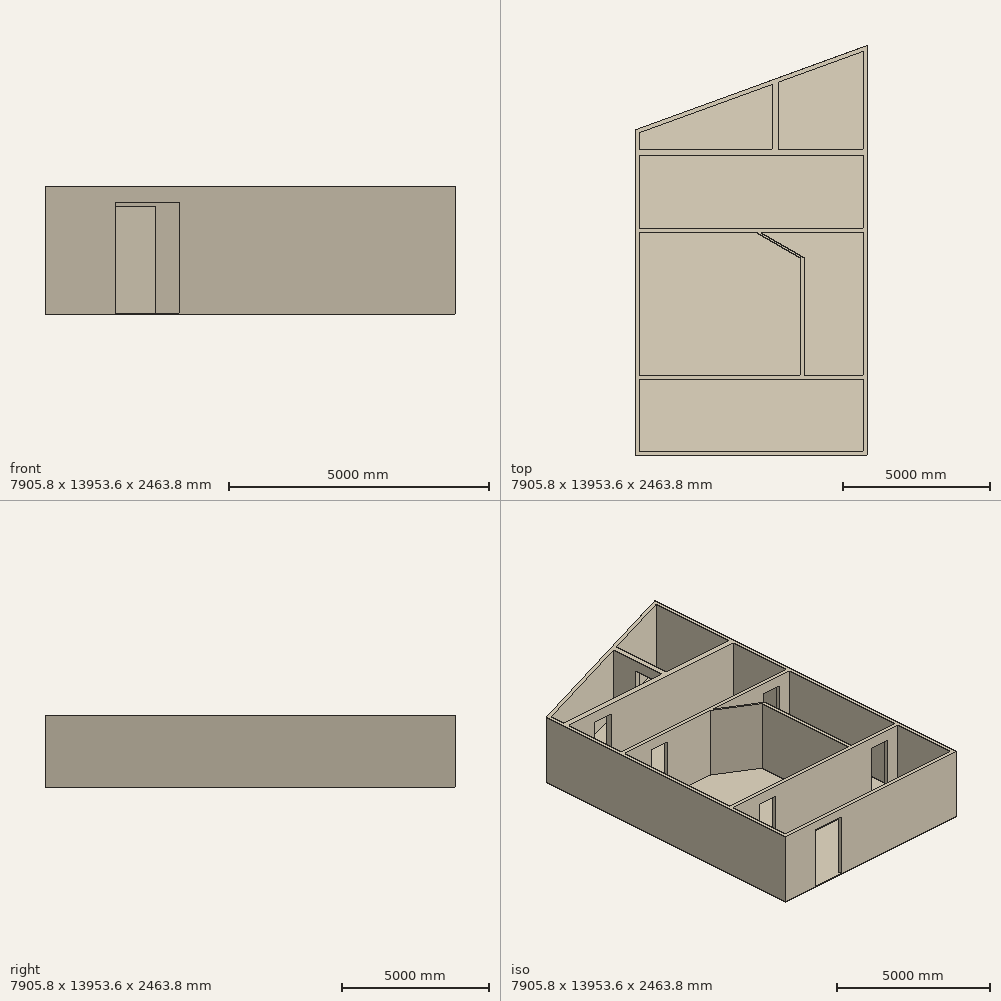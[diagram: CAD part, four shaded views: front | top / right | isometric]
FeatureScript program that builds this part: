
annotation { "Feature Type Name" : "Feature", "Feature Type Description" : "" }
export const myFeature = defineFeature(function(context is Context, id is Id, definition is map)
    precondition{}
    {
        {
            var Q0;
            Q0=qCreatedBy(makeId("Top.planeOp"),FACE);
            var sketch = newSketch(context, id + "F0", { "sketchPlane" : qUnion([Q0])});
            skLineSegment(sketch, "E0", {"start": v(0, 0) * mm, "end": v(0, -11076.15) * mm});
            skLineSegment(sketch, "E1", {"start": v(0, -11076.15) * mm, "end": v(7905.75, -11076.15) * mm});
            skLineSegment(sketch, "E2", {"start": v(7905.75, -11076.15) * mm, "end": v(7905.75, 2877.46) * mm});
            skLineSegment(sketch, "E3", {"start": v(7905.75, 2877.46) * mm, "end": v(0, 0) * mm});
            skLineSegment(sketch, "E4.0", {"start": v(139.7, -97.82) * mm, "end": v(139.7, -10936.45) * mm});
            skLineSegment(sketch, "E4.1", {"start": v(7766.05, 2677.95) * mm, "end": v(139.7, -97.82) * mm});
            skLineSegment(sketch, "E4.2", {"start": v(7766.05, -10936.45) * mm, "end": v(7766.05, 2677.95) * mm});
            skLineSegment(sketch, "E4.3", {"start": v(139.7, -10936.45) * mm, "end": v(7766.05, -10936.45) * mm});
            skLineSegment(sketch, "E5", {"start": v(139.7, -8498.05) * mm, "end": v(7766.05, -8498.05) * mm});
            skLineSegment(sketch, "E6", {"start": v(139.7, -8358.35) * mm, "end": v(7766.05, -8358.35) * mm});
            skLineSegment(sketch, "E7", {"start": v(139.7, -3341.85) * mm, "end": v(7766.05, -3341.85) * mm});
            skLineSegment(sketch, "E8", {"start": v(139.7, -3481.55) * mm, "end": v(7766.05, -3481.55) * mm});
            skLineSegment(sketch, "E9", {"start": v(139.7, -674.85) * mm, "end": v(7766.05, -674.85) * mm});
            skLineSegment(sketch, "E10", {"start": v(139.7, -878.05) * mm, "end": v(7766.05, -878.05) * mm});
            skLineSegment(sketch, "E11", {"start": v(4667.25, -674.85) * mm, "end": v(4667.25, 1550.07) * mm});
            skLineSegment(sketch, "E12", {"start": v(4870.45, -674.85) * mm, "end": v(4870.45, 1624.03) * mm});
            skLineSegment(sketch, "E13", {"start": v(5626.1, -4361.44) * mm, "end": v(5626.1, -8358.35) * mm});
            skLineSegment(sketch, "E14", {"start": v(5765.8, -4361.44) * mm, "end": v(5765.8, -8358.35) * mm});
            skLineSegment(sketch, "E15", {"start": v(5626.1, -4361.44) * mm, "end": v(5765.8, -4361.44) * mm});
            skLineSegment(sketch, "E16", {"start": v(5626.1, -4361.44) * mm, "end": v(4102.1, -3481.55) * mm});
            skLineSegment(sketch, "E17", {"start": v(4102.1, -3481.55) * mm, "end": v(4241.8, -3481.55) * mm});
            skLineSegment(sketch, "E18", {"start": v(4241.8, -3481.55) * mm, "end": v(5765.8, -4361.44) * mm});
            skSolve(sketch);
        }
        {
            var Q0;
            Q0=makeQuery(id+"F0.imprint","IMPRINT",FACE,{"disambiguationData":[TD([[makeQuery(id+"F0.imprint","IMPRINT",EDGE,{"derivedFrom":sQuery(id+"F0.wireOp",EDGE,"E0")}),1.0]])]});
            var Q1;
            {var subQ0=sQuery(id+"F0.wireOp",EDGE,"E10");Q1=makeQuery(id+"F0.imprint","IMPRINT",FACE,{"disambiguationData":[TD([[makeQuery(id+"F0.imprint","IMPRINT",EDGE,{"derivedFrom":subQ0}),1.0]])]});}
            var Q2;
            {var subQ1=sQuery(id+"F0.wireOp",EDGE,"E11");Q2=makeQuery(id+"F0.imprint","IMPRINT",FACE,{"disambiguationData":[TD([[makeQuery(id+"F0.imprint","IMPRINT",EDGE,{"derivedFrom":subQ1}),-1.0]])]});}
            var Q3;
            {var subQ7=sQuery(id+"F0.wireOp",EDGE,"E7");Q3=makeQuery(id+"F0.imprint","IMPRINT",FACE,{"disambiguationData":[TD([[makeQuery(id+"F0.imprint","IMPRINT",EDGE,{"derivedFrom":subQ7}),-1.0]])]});}
            var Q4;
            {var subQ1=sQuery(id+"F0.wireOp",EDGE,"E13");Q4=makeQuery(id+"F0.imprint","IMPRINT",FACE,{"disambiguationData":[TD([[makeQuery(id+"F0.imprint","IMPRINT",EDGE,{"derivedFrom":subQ1}),1.0]])]});}
            var Q5;
            {var subQ5=sQuery(id+"F0.wireOp",EDGE,"E5");Q5=makeQuery(id+"F0.imprint","IMPRINT",FACE,{"disambiguationData":[TD([[makeQuery(id+"F0.imprint","IMPRINT",EDGE,{"derivedFrom":subQ5}),1.0]])]});}
            var Q6;
            Q6=makeQuery(id+"F0.imprint","IMPRINT",FACE,{"disambiguationData":[TD([[makeQuery(id+"F0.imprint","IMPRINT",EDGE,{"derivedFrom":sQuery(id+"F0.wireOp",EDGE,"E15")}),1.0]])]});
            extrude(context, id + "F1", {"entities" : qUnion([Q0, Q1, Q2, Q3, Q4, Q5, Q6]), "depth" : 2438.4 * mm});
        }
        {
            var Q0;
            Q0=qCreatedBy(makeId("Top.planeOp"),FACE);
            var sketch = newSketch(context, id + "F2", { "sketchPlane" : qUnion([Q0])});
            skLineSegment(sketch, "E19.0", {"start": v(7905.75, 2877.46) * mm, "end": v(0, 0) * mm});
            skLineSegment(sketch, "E20.1", {"start": v(7905.75, -11076.15) * mm, "end": v(7905.75, 2877.46) * mm});
            skLineSegment(sketch, "E21.2", {"start": v(0, -11076.15) * mm, "end": v(7905.75, -11076.15) * mm});
            skLineSegment(sketch, "E22.3", {"start": v(0, 0) * mm, "end": v(0, -11076.15) * mm});
            skSolve(sketch);
        }
        {
            var Q0;
            Q0 = qSketchRegion(id + "F2", true);
            extrude(context, id + "F3", {"entities" : qUnion([Q0]), "operationType" : NewBodyOperationType.ADD, "oppositeDirection" : true, "depth" : 25.4 * mm});
        }
        {
            var Q0;
            Q0=makeQuery(id+"F1.opExtrude","SWEPT_FACE",FACE,{"disambiguationData":[OSD([sQuery(id+"F0.wireOp",EDGE,"E5")])]});
            var sketch = newSketch(context, id + "F4", { "sketchPlane" : qUnion([Q0])});
            skLineSegment(sketch, "E23.bottom", {"start": v(1358.9, 0) * mm, "end": v(2120.9, 0) * mm});
            skLineSegment(sketch, "E23.top", {"start": v(1358.9, 2057.4) * mm, "end": v(2120.9, 2057.4) * mm});
            skLineSegment(sketch, "E23.left", {"start": v(1358.9, 0) * mm, "end": v(1358.9, 2057.4) * mm});
            skLineSegment(sketch, "E23.right", {"start": v(2120.9, 0) * mm, "end": v(2120.9, 2057.4) * mm});
            skLineSegment(sketch, "E24.bottom", {"start": v(6546.85, 0) * mm, "end": v(7308.85, 0) * mm});
            skLineSegment(sketch, "E24.top", {"start": v(6546.85, 2057.4) * mm, "end": v(7308.85, 2057.4) * mm});
            skLineSegment(sketch, "E24.left", {"start": v(6546.85, 0) * mm, "end": v(6546.85, 2057.4) * mm});
            skLineSegment(sketch, "E24.right", {"start": v(7308.85, 0) * mm, "end": v(7308.85, 2057.4) * mm});
            skSolve(sketch);
        }
        {
            var Q0;
            {var subQ0=sQuery(id+"F0.wireOp",EDGE,"E8");Q0=makeQuery(id+"F1.opExtrude","SWEPT_FACE",FACE,{"disambiguationData":[OSD([subQ0]),TDD([makeQuery(id+"F0.imprint","IMPRINT",EDGE,{"disambiguationData":[TD([[makeQuery(id+"F0.imprint","INTERSECT",VERTEX,{"derivedFrom":[sQuery(id+"F0.wireOp",EDGE,"E4.0"),subQ0]}),-1.0]])],"derivedFrom":subQ0})])]});}
            var sketch = newSketch(context, id + "F5", { "sketchPlane" : qUnion([Q0])});
            skLineSegment(sketch, "E25.bottom", {"start": v(1358.9, 0) * mm, "end": v(2120.9, 0) * mm});
            skLineSegment(sketch, "E25.top", {"start": v(1358.9, 2057.4) * mm, "end": v(2120.9, 2057.4) * mm});
            skLineSegment(sketch, "E25.left", {"start": v(1358.9, 0) * mm, "end": v(1358.9, 2057.4) * mm});
            skLineSegment(sketch, "E25.right", {"start": v(2120.9, 0) * mm, "end": v(2120.9, 2057.4) * mm});
            skLineSegment(sketch, "E26.bottom", {"start": v(6546.85, 0) * mm, "end": v(7308.85, 0) * mm});
            skLineSegment(sketch, "E26.top", {"start": v(6546.85, 2057.4) * mm, "end": v(7308.85, 2057.4) * mm});
            skLineSegment(sketch, "E26.left", {"start": v(6546.85, 0) * mm, "end": v(6546.85, 2057.4) * mm});
            skLineSegment(sketch, "E26.right", {"start": v(7308.85, 0) * mm, "end": v(7308.85, 2057.4) * mm});
            skSolve(sketch);
        }
        {
            var Q0;
            Q0=makeQuery(id+"F1.opExtrude","SWEPT_FACE",FACE,{"disambiguationData":[OSD([sQuery(id+"F0.wireOp",EDGE,"E10")])]});
            var sketch = newSketch(context, id + "F6", { "sketchPlane" : qUnion([Q0])});
            skLineSegment(sketch, "E27.bottom", {"start": v(1358.9, 0) * mm, "end": v(2120.9, 0) * mm});
            skLineSegment(sketch, "E27.top", {"start": v(1358.9, 2057.4) * mm, "end": v(2120.9, 2057.4) * mm});
            skLineSegment(sketch, "E27.left", {"start": v(1358.9, 0) * mm, "end": v(1358.9, 2057.4) * mm});
            skLineSegment(sketch, "E27.right", {"start": v(2120.9, 0) * mm, "end": v(2120.9, 2057.4) * mm});
            skSolve(sketch);
        }
        {
            var Q0;
            Q0=makeQuery(id+"F1.opExtrude","SWEPT_FACE",FACE,{"disambiguationData":[OSD([sQuery(id+"F0.wireOp",EDGE,"E11")])]});
            var sketch = newSketch(context, id + "F7", { "sketchPlane" : qUnion([Q0])});
            skLineSegment(sketch, "E28.bottom", {"start": v(217.65, 0) * mm, "end": v(-544.35, 0) * mm});
            skLineSegment(sketch, "E28.top", {"start": v(217.65, 2057.4) * mm, "end": v(-544.35, 2057.4) * mm});
            skLineSegment(sketch, "E28.left", {"start": v(217.65, 0) * mm, "end": v(217.65, 2057.4) * mm});
            skLineSegment(sketch, "E28.right", {"start": v(-544.35, 0) * mm, "end": v(-544.35, 2057.4) * mm});
            skSolve(sketch);
        }
        {
            var Q0;
            Q0=makeQuery(id+"F5.imprint","IMPRINT",FACE,{"disambiguationData":[TD([[makeQuery(id+"F5.imprint","IMPRINT",EDGE,{"derivedFrom":sQuery(id+"F5.wireOp",EDGE,"E26.bottom")}),1.0]])]});
            var Q1;
            Q1=makeQuery(id+"F5.imprint","IMPRINT",FACE,{"disambiguationData":[TD([[makeQuery(id+"F5.imprint","IMPRINT",EDGE,{"derivedFrom":sQuery(id+"F5.wireOp",EDGE,"E25.bottom")}),1.0]])]});
            var Q2;
            Q2=makeQuery(id+"F6.imprint","IMPRINT",FACE,{"disambiguationData":[TD([[makeQuery(id+"F6.imprint","IMPRINT",EDGE,{"derivedFrom":sQuery(id+"F6.wireOp",EDGE,"E27.bottom")}),1.0]])]});
            var Q3;
            Q3=makeQuery(id+"F4.imprint","IMPRINT",FACE,{"disambiguationData":[TD([[makeQuery(id+"F4.imprint","IMPRINT",EDGE,{"derivedFrom":sQuery(id+"F4.wireOp",EDGE,"E23.bottom")}),1.0]])]});
            var Q4;
            Q4=makeQuery(id+"F4.imprint","IMPRINT",FACE,{"disambiguationData":[TD([[makeQuery(id+"F4.imprint","IMPRINT",EDGE,{"derivedFrom":sQuery(id+"F4.wireOp",EDGE,"E24.bottom")}),1.0]])]});
            extrude(context, id + "F8", {"entities" : qUnion([Q0, Q1, Q2, Q3, Q4]), "operationType" : NewBodyOperationType.REMOVE, "endBound" : BoundingType.UP_TO_NEXT, "oppositeDirection" : true, "depth" : 25.4 * mm});
        }
        {
            var Q0;
            Q0=makeQuery(id+"F7.imprint","IMPRINT",FACE,{"disambiguationData":[TD([[makeQuery(id+"F7.imprint","IMPRINT",EDGE,{"derivedFrom":sQuery(id+"F7.wireOp",EDGE,"E28.bottom")}),-1.0]])]});
            extrude(context, id + "F9", {"entities" : qUnion([Q0]), "operationType" : NewBodyOperationType.REMOVE, "endBound" : BoundingType.UP_TO_NEXT, "oppositeDirection" : true, "depth" : 25.4 * mm});
        }
        {
            var Q0;
            Q0=makeQuery(id+"F1.opExtrude","SWEPT_FACE",FACE,{"disambiguationData":[OSD([sQuery(id+"F0.wireOp",EDGE,"E4.3")])]});
            var sketch = newSketch(context, id + "F10", { "sketchPlane" : qUnion([Q0])});
            skLineSegment(sketch, "E29.bottom", {"start": v(-2578.1, 0) * mm, "end": v(-1358.9, 0) * mm});
            skLineSegment(sketch, "E29.top", {"start": v(-2578.1, 2133.6) * mm, "end": v(-1358.9, 2133.6) * mm});
            skLineSegment(sketch, "E29.left", {"start": v(-2578.1, 0) * mm, "end": v(-2578.1, 2133.6) * mm});
            skLineSegment(sketch, "E29.right", {"start": v(-1358.9, 0) * mm, "end": v(-1358.9, 2133.6) * mm});
            skSolve(sketch);
        }
        {
            var Q0;
            Q0=makeQuery(id+"F10.imprint","IMPRINT",FACE,{"disambiguationData":[TD([[makeQuery(id+"F10.imprint","IMPRINT",EDGE,{"derivedFrom":sQuery(id+"F10.wireOp",EDGE,"E29.bottom")}),-1.0]])]});
            extrude(context, id + "F11", {"entities" : qUnion([Q0]), "operationType" : NewBodyOperationType.REMOVE, "endBound" : BoundingType.UP_TO_NEXT, "oppositeDirection" : true, "depth" : 30.48 * mm});
        }
    });
